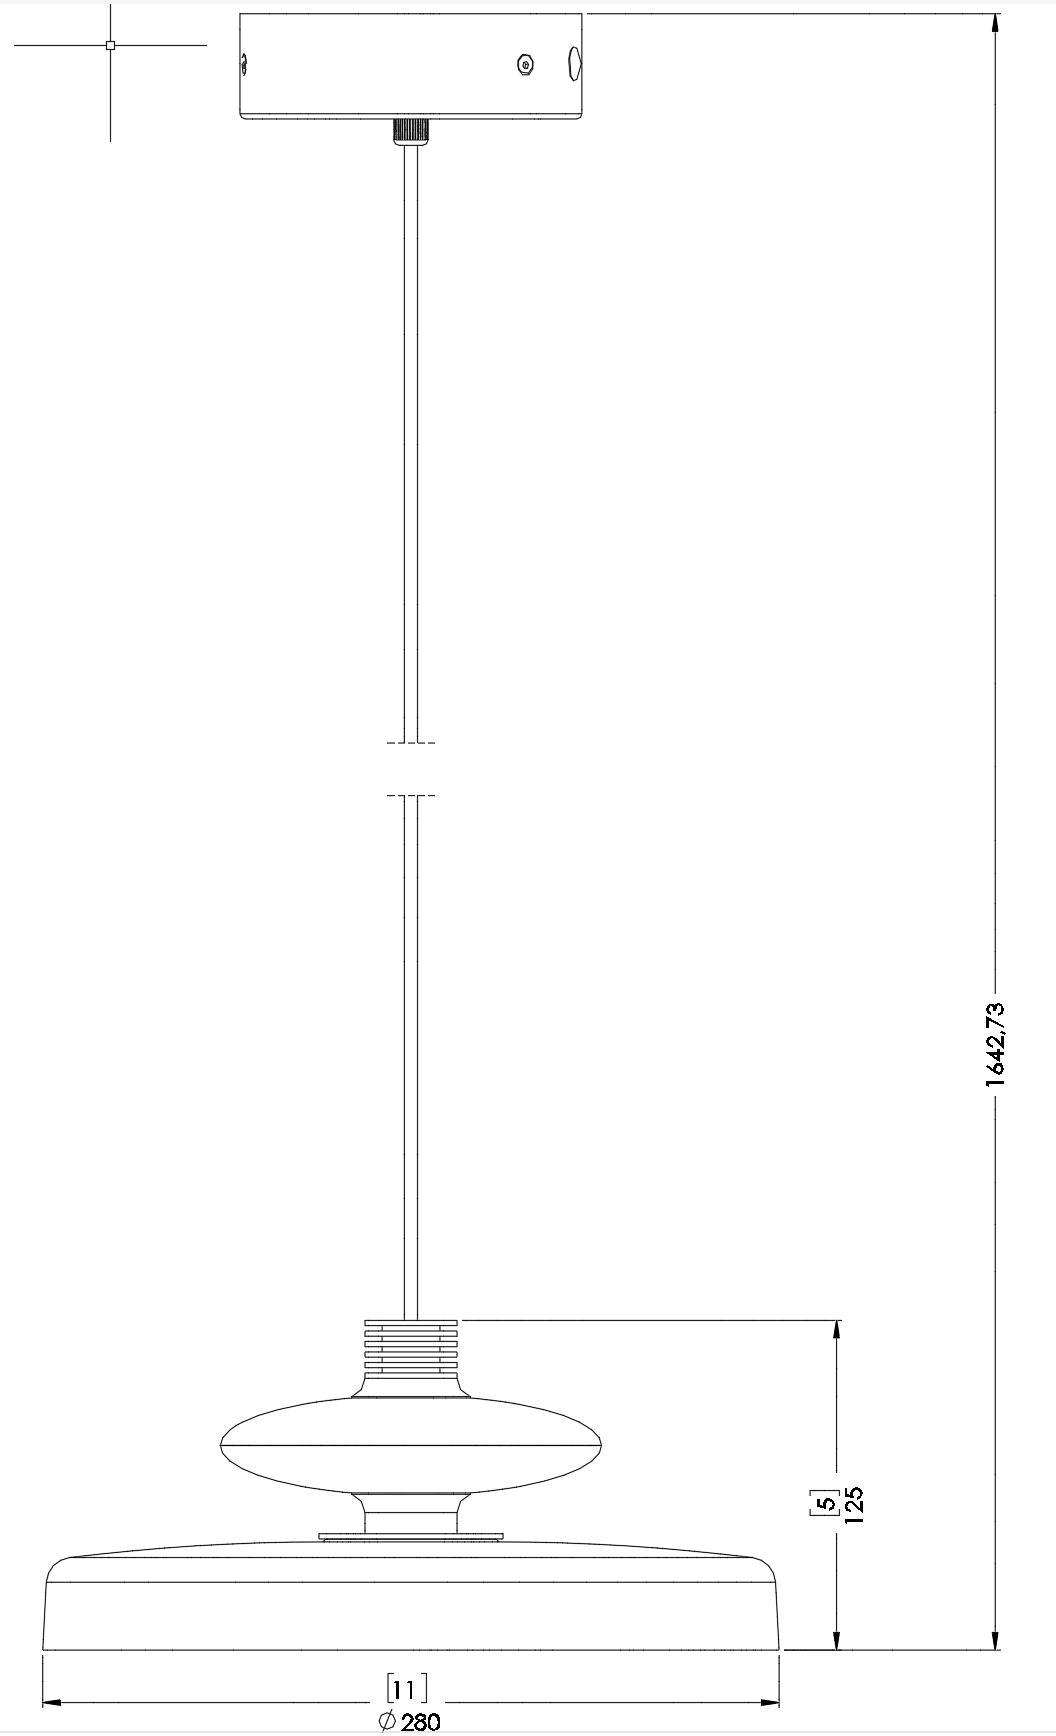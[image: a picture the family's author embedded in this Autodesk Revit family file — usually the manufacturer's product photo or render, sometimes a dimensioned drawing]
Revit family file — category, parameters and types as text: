
# Revit family: TREAD-Table
name_source: partatom
category: Lighting Fixtures
units: mm (PartAtom-declared; Revit-internal decimal feet)

## family parameters
Always vertical = Yes
Cut with Voids When Loaded = No
Light Source = No
OmniClass Number = 23.80.70.00
OmniClass Title = Lighting
Part Type = Normal
Room Calculation Point = No
Round Connector Dimension = Use Diameter
Shared = No
Work Plane-Based = Yes

## types (1)
- TREAD LT
    Bulb Diametr = 15 mm  [stored 0.0492126 ft]
    Country = Europe
    Default Elevation = 1219 mm
    Depth = 20 mm  [stored 0.0656168 ft]
    Description = TABLE LAMP
    Designer = Studio Debonademeo
    Manufacturer = Vistosi
    Manufacturer country = Italy
    Model = TREAD
    Type Comments = Studio Debonademeo
    URL = https://vistosi.com
    URL Product Page = https://vistosi.it
    Width = 15 mm  [stored 0.0492126 ft]

note: [stored X ft] marks values corroborated as IEEE doubles in the binary element streams (Revit-internal decimal feet)

## geometry (parser evidence)
native form markers: Sweep x6
no freeform markers — native parametric forms only
